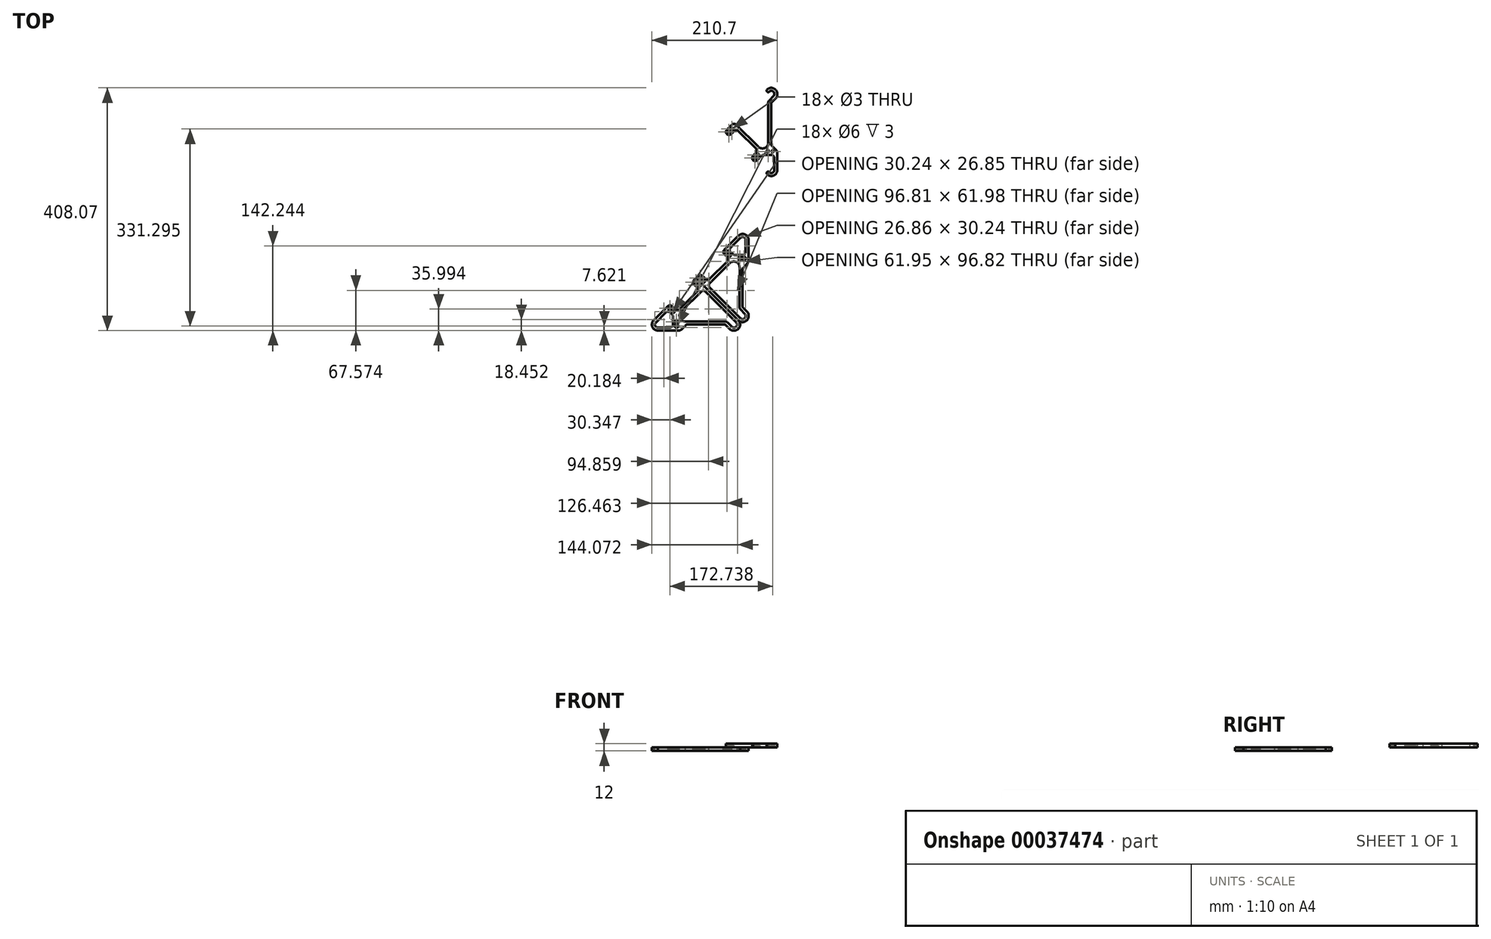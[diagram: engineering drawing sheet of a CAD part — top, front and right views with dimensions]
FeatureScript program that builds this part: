
annotation { "Feature Type Name" : "Feature", "Feature Type Description" : "" }
export const myFeature = defineFeature(function(context is Context, id is Id, definition is map)
    precondition{}
    {
        {
            var Q0;
            Q0=qCreatedBy(makeId("Top.planeOp"),FACE);
            var sketch = newSketch(context, id + "F0", { "sketchPlane" : qUnion([Q0])});
            skLineSegment(sketch, "E0", {"start": v(-29.78, -43.68) * mm, "end": v(-29.78, -43.68) * mm, "construction": true});
            skLineSegment(sketch, "E1", {"start": v(-29.78, -50.68) * mm, "end": v(-29.78, -50.68) * mm, "construction": true});
            skCircle(sketch, "E2", {"center": v(-40.77, -19.32) * mm, "radius": 1.5 * mm, "construction": true});
            skCircle(sketch, "E3", {"center": v(-35.83, -24.28) * mm, "radius": 1.5 * mm, "construction": true});
            skCircle(sketch, "E4", {"center": v(-29.78, -49.09) * mm, "radius": 1.5 * mm});
            skCircle(sketch, "E5", {"center": v(8.01, 19.57) * mm, "radius": 1.5 * mm});
            skCircle(sketch, "E6", {"center": v(3.07, 24.51) * mm, "radius": 1.5 * mm});
            skPoint(sketch, "E7.visualSharp", {"position": v(-33.33, -49.63) * mm});
            skCircle(sketch, "E8", {"center": v(-40.77, -19.32) * mm, "radius": 3 * mm});
            skCircle(sketch, "E9", {"center": v(-35.83, -24.28) * mm, "radius": 3 * mm});
            skCircle(sketch, "E10", {"center": v(-29.78, -49.09) * mm, "radius": 3 * mm});
            skCircle(sketch, "E11", {"center": v(3.07, 24.51) * mm, "radius": 3 * mm});
            skCircle(sketch, "E12", {"center": v(8.01, 19.57) * mm, "radius": 3 * mm});
            skCircle(sketch, "E13", {"center": v(-29.78, -42.09) * mm, "radius": 3 * mm});
            skArc(sketch, "E14", {"start": v(-67.9, -39.36) * mm, "mid": v(-70.46, -50.28) * mm, "end": v(-61.27, -56.7) * mm});
            skLineSegment(sketch, "E15", {"start": v(-67.9, -39.36) * mm, "end": v(-44.25, -15.73) * mm});
            skLineSegment(sketch, "E16", {"start": v(-32.29, -20.75) * mm, "end": v(-37.03, -16) * mm});
            skLineSegment(sketch, "E17", {"start": v(-25.1, -20.87) * mm, "end": v(4.62, 8.82) * mm});
            skLineSegment(sketch, "E18", {"start": v(-32.29, -20.75) * mm, "end": v(-32.16, -20.87) * mm});
            skLineSegment(sketch, "E19", {"start": v(4.47, 16.03) * mm, "end": v(4.62, 15.89) * mm});
            skLineSegment(sketch, "E20", {"start": v(4.47, 16.03) * mm, "end": v(-0.47, 20.98) * mm});
            skLineSegment(sketch, "E21", {"start": v(6.6, 28.05) * mm, "end": v(74.24, -39.64) * mm});
            skArc(sketch, "E22.filletArc", {"start": v(-32.16, -20.87) * mm, "mid": v(-28.63, -22.34) * mm, "end": v(-25.1, -20.87) * mm});
            skArc(sketch, "E23.filletArc", {"start": v(4.62, 8.82) * mm, "mid": v(6.08, 12.35) * mm, "end": v(4.62, 15.89) * mm});
            skLineSegment(sketch, "E24", {"start": v(64.59, -56.7) * mm, "end": v(67.17, -56.7) * mm});
            skPoint(sketch, "E25.visualSharp", {"position": v(91.3, -56.7) * mm});
            skArc(sketch, "E25.filletArc", {"start": v(67.17, -56.7) * mm, "mid": v(76.4, -50.54) * mm, "end": v(74.24, -39.64) * mm});
            skPoint(sketch, "E26.newPointA", {"position": v(59.7, -46.7) * mm});
            skPoint(sketch, "E27.newPointA", {"position": v(-24.2, -46.7) * mm});
            skLineSegment(sketch, "E28", {"start": v(-73.24, -63.03) * mm, "end": v(81.04, -63.03) * mm});
            skLineSegment(sketch, "E29.0", {"start": v(-64.61, -43.15) * mm, "end": v(-47.87, -26.41) * mm});
            skLineSegment(sketch, "E30", {"start": v(61.05, -55.24) * mm, "end": v(53.99, -48.17) * mm});
            skLineSegment(sketch, "E31", {"start": v(-15.01, -48.17) * mm, "end": v(-22.1, -55.24) * mm});
            skPoint(sketch, "E32.visualSharp", {"position": v(52.52, -46.7) * mm});
            skArc(sketch, "E32.filletArc", {"start": v(53.99, -48.17) * mm, "mid": v(52.36, -47.09) * mm, "end": v(50.45, -46.7) * mm});
            skPoint(sketch, "E33.newPointB", {"position": v(-61.27, -56.7) * mm});
            skArc(sketch, "E33.filletArc", {"start": v(61.05, -55.24) * mm, "mid": v(62.67, -56.33) * mm, "end": v(64.59, -56.7) * mm});
            skLineSegment(sketch, "E34", {"start": v(-25.63, -56.7) * mm, "end": v(-61.27, -56.7) * mm});
            skPoint(sketch, "E35.visualSharp", {"position": v(-23.56, -56.7) * mm});
            skArc(sketch, "E35.filletArc", {"start": v(-25.63, -56.7) * mm, "mid": v(-23.71, -56.33) * mm, "end": v(-22.1, -55.24) * mm});
            skArc(sketch, "E36", {"start": v(-44.25, -15.73) * mm, "mid": v(-40.58, -14.3) * mm, "end": v(-37.03, -16) * mm});
            skCircle(sketch, "E37", {"center": v(-35.83, -24.28) * mm, "radius": 1.5 * mm});
            skCircle(sketch, "E38", {"center": v(-40.77, -19.32) * mm, "radius": 1.5 * mm});
            skCircle(sketch, "E39", {"center": v(-29.78, -42.09) * mm, "radius": 1.5 * mm});
            skArc(sketch, "E40", {"start": v(-0.47, 20.98) * mm, "mid": v(-0.47, 28.05) * mm, "end": v(6.6, 28.05) * mm});
            skLineSegment(sketch, "E41", {"start": v(63.42, -50.52) * mm, "end": v(56.08, -43.17) * mm});
            skPoint(sketch, "E42.visualSharp", {"position": v(54.61, -41.7) * mm});
            skArc(sketch, "E42.filletArc", {"start": v(56.08, -43.17) * mm, "mid": v(54.45, -42.08) * mm, "end": v(52.54, -41.7) * mm});
            skArc(sketch, "E43.0", {"start": v(67.17, -51.7) * mm, "mid": v(71.79, -48.62) * mm, "end": v(70.7, -43.17) * mm});
            skLineSegment(sketch, "E44", {"start": v(70.7, -43.17) * mm, "end": v(70.7, -43.17) * mm});
            skLineSegment(sketch, "E45", {"start": v(66.35, -51.7) * mm, "end": v(67.17, -51.7) * mm});
            skArc(sketch, "E46", {"start": v(66.35, -51.7) * mm, "mid": v(64.77, -51.4) * mm, "end": v(63.42, -50.52) * mm});
            skArc(sketch, "E47.filletArc", {"start": v(18.76, 8.81) * mm, "mid": v(15.22, 10.28) * mm, "end": v(11.69, 8.81) * mm});
            skArc(sketch, "E48.filletArc", {"start": v(-64.61, -43.15) * mm, "mid": v(-65.7, -48.6) * mm, "end": v(-61.08, -51.68) * mm});
            skLineSegment(sketch, "E49", {"start": v(18.76, 8.81) * mm, "end": v(70.7, -43.17) * mm});
            skLineSegment(sketch, "E50", {"start": v(-11.48, -46.7) * mm, "end": v(50.45, -46.7) * mm});
            skLineSegment(sketch, "E51", {"start": v(-21.78, -24.63) * mm, "end": v(11.69, 8.81) * mm});
            skLineSegment(sketch, "E52", {"start": v(-47.87, -26.41) * mm, "end": v(-47.75, -26.3) * mm});
            skLineSegment(sketch, "E53", {"start": v(-40.68, -26.3) * mm, "end": v(-37.28, -29.7) * mm});
            skLineSegment(sketch, "E54", {"start": v(-35.82, -33.23) * mm, "end": v(-35.82, -46.68) * mm});
            skPoint(sketch, "E55.visualSharp", {"position": v(-44.21, -22.76) * mm});
            skArc(sketch, "E55.filletArc", {"start": v(-40.68, -26.3) * mm, "mid": v(-44.21, -24.83) * mm, "end": v(-47.75, -26.3) * mm});
            skPoint(sketch, "E56.visualSharp", {"position": v(-35.82, -31.16) * mm});
            skArc(sketch, "E56.filletArc", {"start": v(-35.82, -33.23) * mm, "mid": v(-36.2, -31.32) * mm, "end": v(-37.28, -29.7) * mm});
            skLineSegment(sketch, "E57", {"start": v(-61.08, -51.68) * mm, "end": v(-40.82, -51.68) * mm});
            skPoint(sketch, "E58.visualSharp", {"position": v(-35.82, -51.68) * mm});
            skArc(sketch, "E58.filletArc", {"start": v(-40.82, -51.68) * mm, "mid": v(-37.28, -50.22) * mm, "end": v(-35.82, -46.68) * mm});
            skPoint(sketch, "E59.visualSharp", {"position": v(-13.55, -46.7) * mm});
            skArc(sketch, "E59.filletArc", {"start": v(-11.48, -46.7) * mm, "mid": v(-13.4, -47.09) * mm, "end": v(-15.01, -48.17) * mm});
            skArc(sketch, "E60", {"start": v(-21.78, -24.63) * mm, "mid": v(-23.98, -35.45) * mm, "end": v(-14.88, -41.7) * mm});
            skLineSegment(sketch, "E61", {"start": v(-14.88, -41.7) * mm, "end": v(52.54, -41.7) * mm});
            skSolve(sketch);
        }
        {
            var Q0;
            Q0=makeQuery(id+"F0.imprint","IMPRINT",FACE,{"disambiguationData":[TD([[makeQuery(id+"F0.imprint","IMPRINT",EDGE,{"derivedFrom":sQuery(id+"F0.wireOp",EDGE,"ZM41ytca-vthh-FzDY-ZHJl-nfqRgOJDo8si")}),1.0]])]});
            var Q1;
            {var subQ2=sQuery(id+"F0.wireOp",EDGE,"462530cd-ab40-49ed-864a-d079afbf469e");var subQ6=sQuery(id+"F0.wireOp",EDGE,"E8");var subQ8=makeQuery(id+"F0.imprint","INTERSECT",VERTEX,{"disambiguationData":[OD(0.0)],"derivedFrom":[subQ6,subQ2]});Q1=makeQuery(id+"F0.imprint","IMPRINT",FACE,{"disambiguationData":[TD([[makeQuery(id+"F0.imprint","IMPRINT",EDGE,{"disambiguationData":[TD([[subQ8,-1.0]])],"derivedFrom":subQ6}),-1.0]])]});}
            var Q2;
            {var subQ0=sQuery(id+"F0.wireOp",EDGE,"462530cd-ab40-49ed-864a-d079afbf469e");var subQ1=sQuery(id+"F0.wireOp",EDGE,"E8");var subQ2=makeQuery(id+"F0.imprint","INTERSECT",VERTEX,{"disambiguationData":[OD(0.0)],"derivedFrom":[subQ1,subQ0]});Q2=makeQuery(id+"F0.imprint","IMPRINT",FACE,{"disambiguationData":[TD([[makeQuery(id+"F0.imprint","IMPRINT",EDGE,{"disambiguationData":[TD([[subQ2,-1.0]])],"derivedFrom":subQ1}),1.0]])]});}
            var Q3;
            {var subQ2=sQuery(id+"F0.wireOp",EDGE,"c8d69f50-1bdd-4b81-bc52-8b5ed8a16678");var subQ4=sQuery(id+"F0.wireOp",EDGE,"E9");var subQ6=makeQuery(id+"F0.imprint","INTERSECT",VERTEX,{"disambiguationData":[OD(0.0)],"derivedFrom":[subQ4,subQ2]});Q3=makeQuery(id+"F0.imprint","IMPRINT",FACE,{"disambiguationData":[TD([[makeQuery(id+"F0.imprint","IMPRINT",EDGE,{"disambiguationData":[TD([[subQ6,-1.0]])],"derivedFrom":subQ4}),-1.0]])]});}
            var Q4;
            {var subQ0=sQuery(id+"F0.wireOp",EDGE,"c8d69f50-1bdd-4b81-bc52-8b5ed8a16678");var subQ1=sQuery(id+"F0.wireOp",EDGE,"E9");var subQ2=makeQuery(id+"F0.imprint","INTERSECT",VERTEX,{"disambiguationData":[OD(0.0)],"derivedFrom":[subQ1,subQ0]});Q4=makeQuery(id+"F0.imprint","IMPRINT",FACE,{"disambiguationData":[TD([[makeQuery(id+"F0.imprint","IMPRINT",EDGE,{"disambiguationData":[TD([[subQ2,-1.0]])],"derivedFrom":subQ1}),1.0]])]});}
            var Q5;
            {var subQ3=sQuery(id+"F0.wireOp",EDGE,"462530cd-ab40-49ed-864a-d079afbf469e");var subQ5=sQuery(id+"F0.wireOp",EDGE,"E8");var subQ6=makeQuery(id+"F0.imprint","INTERSECT",VERTEX,{"disambiguationData":[OD(0.0)],"derivedFrom":[subQ5,subQ3]});Q5=makeQuery(id+"F0.imprint","IMPRINT",FACE,{"disambiguationData":[TD([[makeQuery(id+"F0.imprint","IMPRINT",EDGE,{"disambiguationData":[TD([[subQ6,1.0]])],"derivedFrom":subQ5}),-1.0]])]});}
            var Q6;
            {var subQ0=sQuery(id+"F0.wireOp",EDGE,"E16");Q6=makeQuery(id+"F0.imprint","IMPRINT",FACE,{"disambiguationData":[TD([[makeQuery(id+"F0.imprint","IMPRINT",EDGE,{"derivedFrom":subQ0}),1.0]])]});}
            var Q7;
            {var subQ0=sQuery(id+"F0.wireOp",EDGE,"462530cd-ab40-49ed-864a-d079afbf469e");var subQ1=sQuery(id+"F0.wireOp",EDGE,"E8");var subQ2=makeQuery(id+"F0.imprint","INTERSECT",VERTEX,{"disambiguationData":[OD(0.0)],"derivedFrom":[subQ1,subQ0]});Q7=makeQuery(id+"F0.imprint","IMPRINT",FACE,{"disambiguationData":[TD([[makeQuery(id+"F0.imprint","IMPRINT",EDGE,{"disambiguationData":[TD([[subQ2,1.0]])],"derivedFrom":subQ1}),1.0]])]});}
            var Q8;
            {var subQ0=sQuery(id+"F0.wireOp",EDGE,"c8d69f50-1bdd-4b81-bc52-8b5ed8a16678");var subQ1=sQuery(id+"F0.wireOp",EDGE,"E9");var subQ2=makeQuery(id+"F0.imprint","INTERSECT",VERTEX,{"disambiguationData":[OD(0.0)],"derivedFrom":[subQ1,subQ0]});Q8=makeQuery(id+"F0.imprint","IMPRINT",FACE,{"disambiguationData":[TD([[makeQuery(id+"F0.imprint","IMPRINT",EDGE,{"disambiguationData":[TD([[subQ2,1.0]])],"derivedFrom":subQ1}),1.0]])]});}
            var Q9;
            {var subQ0=sQuery(id+"F0.wireOp",EDGE,"e0227538-d441-4e94-826a-84f47eb18c94");var subQ1=makeQuery(id+"F0.imprint","INTERSECT",VERTEX,{"derivedFrom":[sQuery(id+"F0.wireOp",EDGE,"E10"),subQ0]});Q9=makeQuery(id+"F0.imprint","IMPRINT",FACE,{"disambiguationData":[TD([[makeQuery(id+"F0.imprint","IMPRINT",EDGE,{"disambiguationData":[TD([[subQ1,1.0]])],"derivedFrom":subQ0}),1.0]])]});}
            var Q10;
            Q10=makeQuery(id+"F0.imprint","IMPRINT",FACE,{"disambiguationData":[TD([[makeQuery(id+"F0.imprint","IMPRINT",EDGE,{"derivedFrom":sQuery(id+"F0.wireOp",EDGE,"E13")}),1.0]])]});
            var Q11;
            {var subQ0=sQuery(id+"F0.wireOp",EDGE,"E20");Q11=makeQuery(id+"F0.imprint","IMPRINT",FACE,{"disambiguationData":[TD([[makeQuery(id+"F0.imprint","IMPRINT",EDGE,{"derivedFrom":subQ0}),-1.0]])]});}
            var Q12;
            {var subQ2=sQuery(id+"F0.wireOp",EDGE,"98726ccb-f84b-485e-b86c-f66cbd653361");var subQ4=sQuery(id+"F0.wireOp",EDGE,"E12");var subQ6=makeQuery(id+"F0.imprint","INTERSECT",VERTEX,{"disambiguationData":[OD(0.0)],"derivedFrom":[subQ4,subQ2]});Q12=makeQuery(id+"F0.imprint","IMPRINT",FACE,{"disambiguationData":[TD([[makeQuery(id+"F0.imprint","IMPRINT",EDGE,{"disambiguationData":[TD([[subQ6,-1.0]])],"derivedFrom":subQ4}),-1.0]])]});}
            var Q13;
            {var subQ3=sQuery(id+"F0.wireOp",EDGE,"c5cb0bc4-31c7-4bfb-88ff-cc8c739e518f");var subQ7=sQuery(id+"F0.wireOp",EDGE,"E11");var subQ8=makeQuery(id+"F0.imprint","INTERSECT",VERTEX,{"disambiguationData":[OD(0.0)],"derivedFrom":[subQ7,subQ3]});Q13=makeQuery(id+"F0.imprint","IMPRINT",FACE,{"disambiguationData":[TD([[makeQuery(id+"F0.imprint","IMPRINT",EDGE,{"disambiguationData":[TD([[subQ8,1.0]])],"derivedFrom":subQ7}),-1.0]])]});}
            var Q14;
            {var subQ2=sQuery(id+"F0.wireOp",EDGE,"c5cb0bc4-31c7-4bfb-88ff-cc8c739e518f");var subQ6=sQuery(id+"F0.wireOp",EDGE,"E11");var subQ7=makeQuery(id+"F0.imprint","INTERSECT",VERTEX,{"disambiguationData":[OD(0.0)],"derivedFrom":[subQ6,subQ2]});Q14=makeQuery(id+"F0.imprint","IMPRINT",FACE,{"disambiguationData":[TD([[makeQuery(id+"F0.imprint","IMPRINT",EDGE,{"disambiguationData":[TD([[subQ7,-1.0]])],"derivedFrom":subQ6}),-1.0]])]});}
            var Q15;
            {var subQ0=sQuery(id+"F0.wireOp",EDGE,"E21");var subQ1=sQuery(id+"F0.wireOp",EDGE,"98726ccb-f84b-485e-b86c-f66cbd653361");var subQ2=makeQuery(id+"F0.imprint","INTERSECT",VERTEX,{"derivedFrom":[subQ1,subQ0]});Q15=makeQuery(id+"F0.imprint","IMPRINT",FACE,{"disambiguationData":[TD([[makeQuery(id+"F0.imprint","IMPRINT",EDGE,{"disambiguationData":[TD([[subQ2,1.0]])],"derivedFrom":subQ1}),-1.0]])]});}
            var Q16;
            {var subQ0=sQuery(id+"F0.wireOp",EDGE,"98726ccb-f84b-485e-b86c-f66cbd653361");var subQ1=sQuery(id+"F0.wireOp",EDGE,"E12");var subQ2=makeQuery(id+"F0.imprint","INTERSECT",VERTEX,{"disambiguationData":[OD(0.0)],"derivedFrom":[subQ1,subQ0]});Q16=makeQuery(id+"F0.imprint","IMPRINT",FACE,{"disambiguationData":[TD([[makeQuery(id+"F0.imprint","IMPRINT",EDGE,{"disambiguationData":[TD([[subQ2,1.0]])],"derivedFrom":subQ1}),1.0]])]});}
            var Q17;
            {var subQ0=sQuery(id+"F0.wireOp",EDGE,"c5cb0bc4-31c7-4bfb-88ff-cc8c739e518f");var subQ1=sQuery(id+"F0.wireOp",EDGE,"E11");var subQ2=makeQuery(id+"F0.imprint","INTERSECT",VERTEX,{"disambiguationData":[OD(0.0)],"derivedFrom":[subQ1,subQ0]});Q17=makeQuery(id+"F0.imprint","IMPRINT",FACE,{"disambiguationData":[TD([[makeQuery(id+"F0.imprint","IMPRINT",EDGE,{"disambiguationData":[TD([[subQ2,1.0]])],"derivedFrom":subQ1}),1.0]])]});}
            var Q18;
            Q18=makeQuery(id+"F0.imprint","IMPRINT",FACE,{"disambiguationData":[TD([[makeQuery(id+"F0.imprint","IMPRINT",EDGE,{"derivedFrom":sQuery(id+"F0.wireOp",EDGE,"E9")}),1.0]])]});
            var Q19;
            Q19=makeQuery(id+"F0.imprint","IMPRINT",FACE,{"disambiguationData":[TD([[makeQuery(id+"F0.imprint","IMPRINT",EDGE,{"derivedFrom":sQuery(id+"F0.wireOp",EDGE,"E4")}),-1.0]])]});
            var Q20;
            Q20=makeQuery(id+"F0.imprint","IMPRINT",FACE,{"disambiguationData":[TD([[makeQuery(id+"F0.imprint","IMPRINT",EDGE,{"derivedFrom":sQuery(id+"F0.wireOp",EDGE,"E8")}),1.0]])]});
            var Q21;
            {var subQ0=sQuery(id+"F0.wireOp",EDGE,"c5cb0bc4-31c7-4bfb-88ff-cc8c739e518f");var subQ1=sQuery(id+"F0.wireOp",EDGE,"E11");var subQ2=makeQuery(id+"F0.imprint","INTERSECT",VERTEX,{"disambiguationData":[OD(0.0)],"derivedFrom":[subQ1,subQ0]});Q21=makeQuery(id+"F0.imprint","IMPRINT",FACE,{"disambiguationData":[TD([[makeQuery(id+"F0.imprint","IMPRINT",EDGE,{"disambiguationData":[TD([[subQ2,-1.0]])],"derivedFrom":subQ1}),1.0]])]});}
            var Q22;
            Q22=makeQuery(id+"F0.imprint","IMPRINT",FACE,{"disambiguationData":[TD([[makeQuery(id+"F0.imprint","IMPRINT",EDGE,{"derivedFrom":sQuery(id+"F0.wireOp",EDGE,"E6")}),-1.0]])]});
            var Q23;
            Q23=makeQuery(id+"F0.imprint","IMPRINT",FACE,{"disambiguationData":[TD([[makeQuery(id+"F0.imprint","IMPRINT",EDGE,{"derivedFrom":sQuery(id+"F0.wireOp",EDGE,"E5")}),-1.0]])]});
            extrude(context, id + "F1", {"entities" : qUnion([Q0, Q1, Q2, Q3, Q4, Q5, Q6, Q7, Q8, Q9, Q10, Q11, Q12, Q13, Q14, Q15, Q16, Q17, Q18, Q19, Q20, Q21, Q22, Q23]), "depth" : 6 * mm});
        }
        {
            var Q0;
            Q0=makeQuery(id+"F0.imprint","IMPRINT",FACE,{"disambiguationData":[TD([[makeQuery(id+"F0.imprint","IMPRINT",EDGE,{"derivedFrom":sQuery(id+"F0.wireOp",EDGE,"E5")}),-1.0]])]});
            var Q1;
            Q1=makeQuery(id+"F0.imprint","IMPRINT",FACE,{"disambiguationData":[TD([[makeQuery(id+"F0.imprint","IMPRINT",EDGE,{"derivedFrom":sQuery(id+"F0.wireOp",EDGE,"E6")}),-1.0]])]});
            var Q2;
            Q2=makeQuery(id+"F0.imprint","IMPRINT",FACE,{"disambiguationData":[TD([[makeQuery(id+"F0.imprint","IMPRINT",EDGE,{"derivedFrom":sQuery(id+"F0.wireOp",EDGE,"E9")}),1.0]])]});
            var Q3;
            Q3=makeQuery(id+"F0.imprint","IMPRINT",FACE,{"disambiguationData":[TD([[makeQuery(id+"F0.imprint","IMPRINT",EDGE,{"derivedFrom":sQuery(id+"F0.wireOp",EDGE,"E8")}),1.0]])]});
            var Q4;
            Q4=makeQuery(id+"F0.imprint","IMPRINT",FACE,{"disambiguationData":[TD([[makeQuery(id+"F0.imprint","IMPRINT",EDGE,{"derivedFrom":sQuery(id+"F0.wireOp",EDGE,"E13")}),1.0]])]});
            var Q5;
            Q5=makeQuery(id+"F0.imprint","IMPRINT",FACE,{"disambiguationData":[TD([[makeQuery(id+"F0.imprint","IMPRINT",EDGE,{"derivedFrom":sQuery(id+"F0.wireOp",EDGE,"E4")}),-1.0]])]});
            extrude(context, id + "F2", {"entities" : qUnion([Q0, Q1, Q2, Q3, Q4, Q5]), "operationType" : NewBodyOperationType.REMOVE, "depth" : 3 * mm});
        }
        {
            var Q0;
            Q0=makeQuery(id+"F1.opExtrude","SWEPT_BODY",BODY,{"disambiguationData":[OSD([sQuery(id+"F0.wireOp",EDGE,"E4"),sQuery(id+"F0.wireOp",EDGE,"E5"),sQuery(id+"F0.wireOp",EDGE,"E6"),sQuery(id+"F0.wireOp",EDGE,"E14"),sQuery(id+"F0.wireOp",EDGE,"E15"),sQuery(id+"F0.wireOp",EDGE,"ZM41ytca-vthh-FzDY-ZHJl-nfqRgOJDo8si"),sQuery(id+"F0.wireOp",EDGE,"E16"),sQuery(id+"F0.wireOp",EDGE,"E17"),sQuery(id+"F0.wireOp",EDGE,"E18"),sQuery(id+"F0.wireOp",EDGE,"E19"),sQuery(id+"F0.wireOp",EDGE,"E20"),sQuery(id+"F0.wireOp",EDGE,"E21"),sQuery(id+"F0.wireOp",EDGE,"E22.filletArc"),sQuery(id+"F0.wireOp",EDGE,"E23.filletArc"),sQuery(id+"F0.wireOp",EDGE,"E24"),sQuery(id+"F0.wireOp",EDGE,"E25.filletArc"),sQuery(id+"F0.wireOp",EDGE,"E29.0"),sQuery(id+"F0.wireOp",EDGE,"Tq16YHEO-ABVa-SyG2-9Bo8-AwoXV9SY9UKx"),sQuery(id+"F0.wireOp",EDGE,"945284af-3b99-493e-8cb3-1405ac220aff.0"),sQuery(id+"F0.wireOp",EDGE,"oyrioEal-kBm6-h2JP-SiMW-HS9MCFllnOTl"),sQuery(id+"F0.wireOp",EDGE,"ebae724b-c969-4c6c-9507-989b8c4a6846.filletArc"),sQuery(id+"F0.wireOp",EDGE,"LpfddLv8-kVTz-Fq9e-9kgw-cFMKpV3D2Iyk"),sQuery(id+"F0.wireOp",EDGE,"93116c20-6c3f-4f09-9b0c-87327ea6eb7f.filletArc"),sQuery(id+"F0.wireOp",EDGE,"eb20cd87-545a-4932-9808-00091d9abf87.filletArc"),sQuery(id+"F0.wireOp",EDGE,"nxfSxcnj-Uu93-61Sm-abPP-Qb7fdRDBaPEy"),sQuery(id+"F0.wireOp",EDGE,"E30"),sQuery(id+"F0.wireOp",EDGE,"xg4YAkpb-tE1s-EWDx-Hdg8-UNIJCbS68nVv"),sQuery(id+"F0.wireOp",EDGE,"E31"),sQuery(id+"F0.wireOp",EDGE,"E32.filletArc"),sQuery(id+"F0.wireOp",EDGE,"E33.filletArc"),sQuery(id+"F0.wireOp",EDGE,"0bd198bb-c4ad-48d3-9048-f5a1ef5a0555.filletArc"),sQuery(id+"F0.wireOp",EDGE,"E34"),sQuery(id+"F0.wireOp",EDGE,"E35.filletArc"),sQuery(id+"F0.wireOp",EDGE,"E36"),sQuery(id+"F0.wireOp",EDGE,"E37"),sQuery(id+"F0.wireOp",EDGE,"E38"),sQuery(id+"F0.wireOp",EDGE,"E39"),sQuery(id+"F0.wireOp",EDGE,"E40"),sQuery(id+"F0.wireOp",EDGE,"E41"),sQuery(id+"F0.wireOp",EDGE,"E42.filletArc"),sQuery(id+"F0.wireOp",EDGE,"E43.0"),sQuery(id+"F0.wireOp",EDGE,"SPg3lbto-ea1S-YeVD-f8W7-4049b7SKFJDl"),sQuery(id+"F0.wireOp",EDGE,"E44"),sQuery(id+"F0.wireOp",EDGE,"E45"),sQuery(id+"F0.wireOp",EDGE,"E46"),sQuery(id+"F0.wireOp",EDGE,"E6A5n6ed-bLnf-SceK-tcdF-HIsw11yMVnoH"),sQuery(id+"F0.wireOp",EDGE,"e5Lx3FfZ-uw1w-XDj5-0S7D-BukahC8YTdbP"),sQuery(id+"F0.wireOp",EDGE,"E47.filletArc"),sQuery(id+"F0.wireOp",EDGE,"0ssyGrfO-lhhZ-gWxP-UVjv-oZQgXaOmNXYf"),sQuery(id+"F0.wireOp",EDGE,"KIXIkL1Q-xUR3-aLeU-v44d-RgIIkf4mlIdz"),sQuery(id+"F0.wireOp",EDGE,"2ec3d0ef-c9eb-4d0e-a1cf-228775a54ac2.filletArc"),sQuery(id+"F0.wireOp",EDGE,"E48.filletArc")])]});
            var Q1;
            Q1=qCreatedBy(makeId("Top.planeOp"),FACE);
            mirror(context, id + "F3", {"entities" : qUnion([Q0]), "mirrorPlane" : qUnion([Q1])});
        }
        {
            var Q0;
            Q0=makeQuery(id+"F1.opExtrude","SWEPT_BODY",BODY,{"disambiguationData":[OSD([sQuery(id+"F0.wireOp",EDGE,"E4"),sQuery(id+"F0.wireOp",EDGE,"E5"),sQuery(id+"F0.wireOp",EDGE,"E6"),sQuery(id+"F0.wireOp",EDGE,"E14"),sQuery(id+"F0.wireOp",EDGE,"E15"),sQuery(id+"F0.wireOp",EDGE,"ZM41ytca-vthh-FzDY-ZHJl-nfqRgOJDo8si"),sQuery(id+"F0.wireOp",EDGE,"E16"),sQuery(id+"F0.wireOp",EDGE,"E17"),sQuery(id+"F0.wireOp",EDGE,"E18"),sQuery(id+"F0.wireOp",EDGE,"E19"),sQuery(id+"F0.wireOp",EDGE,"E20"),sQuery(id+"F0.wireOp",EDGE,"E21"),sQuery(id+"F0.wireOp",EDGE,"E22.filletArc"),sQuery(id+"F0.wireOp",EDGE,"E23.filletArc"),sQuery(id+"F0.wireOp",EDGE,"E24"),sQuery(id+"F0.wireOp",EDGE,"E25.filletArc"),sQuery(id+"F0.wireOp",EDGE,"E29.0"),sQuery(id+"F0.wireOp",EDGE,"Tq16YHEO-ABVa-SyG2-9Bo8-AwoXV9SY9UKx"),sQuery(id+"F0.wireOp",EDGE,"945284af-3b99-493e-8cb3-1405ac220aff.0"),sQuery(id+"F0.wireOp",EDGE,"oyrioEal-kBm6-h2JP-SiMW-HS9MCFllnOTl"),sQuery(id+"F0.wireOp",EDGE,"ebae724b-c969-4c6c-9507-989b8c4a6846.filletArc"),sQuery(id+"F0.wireOp",EDGE,"LpfddLv8-kVTz-Fq9e-9kgw-cFMKpV3D2Iyk"),sQuery(id+"F0.wireOp",EDGE,"93116c20-6c3f-4f09-9b0c-87327ea6eb7f.filletArc"),sQuery(id+"F0.wireOp",EDGE,"eb20cd87-545a-4932-9808-00091d9abf87.filletArc"),sQuery(id+"F0.wireOp",EDGE,"nxfSxcnj-Uu93-61Sm-abPP-Qb7fdRDBaPEy"),sQuery(id+"F0.wireOp",EDGE,"E30"),sQuery(id+"F0.wireOp",EDGE,"xg4YAkpb-tE1s-EWDx-Hdg8-UNIJCbS68nVv"),sQuery(id+"F0.wireOp",EDGE,"E31"),sQuery(id+"F0.wireOp",EDGE,"E32.filletArc"),sQuery(id+"F0.wireOp",EDGE,"E33.filletArc"),sQuery(id+"F0.wireOp",EDGE,"0bd198bb-c4ad-48d3-9048-f5a1ef5a0555.filletArc"),sQuery(id+"F0.wireOp",EDGE,"E34"),sQuery(id+"F0.wireOp",EDGE,"E35.filletArc"),sQuery(id+"F0.wireOp",EDGE,"E36"),sQuery(id+"F0.wireOp",EDGE,"E37"),sQuery(id+"F0.wireOp",EDGE,"E38"),sQuery(id+"F0.wireOp",EDGE,"E39"),sQuery(id+"F0.wireOp",EDGE,"E40"),sQuery(id+"F0.wireOp",EDGE,"E41"),sQuery(id+"F0.wireOp",EDGE,"E42.filletArc"),sQuery(id+"F0.wireOp",EDGE,"E43.0"),sQuery(id+"F0.wireOp",EDGE,"SPg3lbto-ea1S-YeVD-f8W7-4049b7SKFJDl"),sQuery(id+"F0.wireOp",EDGE,"E44"),sQuery(id+"F0.wireOp",EDGE,"E45"),sQuery(id+"F0.wireOp",EDGE,"E46"),sQuery(id+"F0.wireOp",EDGE,"E6A5n6ed-bLnf-SceK-tcdF-HIsw11yMVnoH"),sQuery(id+"F0.wireOp",EDGE,"e5Lx3FfZ-uw1w-XDj5-0S7D-BukahC8YTdbP"),sQuery(id+"F0.wireOp",EDGE,"E47.filletArc"),sQuery(id+"F0.wireOp",EDGE,"0ssyGrfO-lhhZ-gWxP-UVjv-oZQgXaOmNXYf"),sQuery(id+"F0.wireOp",EDGE,"KIXIkL1Q-xUR3-aLeU-v44d-RgIIkf4mlIdz"),sQuery(id+"F0.wireOp",EDGE,"2ec3d0ef-c9eb-4d0e-a1cf-228775a54ac2.filletArc"),sQuery(id+"F0.wireOp",EDGE,"E48.filletArc")])]});
            var Q1;
            Q1=makeQuery(id+"F1.opExtrude","CAP_EDGE",EDGE,{"disambiguationData":[OSD([sQuery(id+"F0.wireOp",EDGE,"E21")])],"isStart":true});
            transform(context, id + "F4", {"entities" : qUnion([Q0]), "transformType" : TransformType.ROTATION, "transformAxis" : qUnion([Q1]), "angle" : 180 * degree, "makeCopy" : false});
        }
        {
            var Q0;
            Q0=qCreatedBy(makeId("Top.planeOp"),FACE);
            var sketch = newSketch(context, id + "F5", { "sketchPlane" : qUnion([Q0])});
            skLineSegment(sketch, "E62", {"start": v(126.55, 244.41) * mm, "end": v(126.55, 244.41) * mm, "construction": true});
            skLineSegment(sketch, "E63", {"start": v(133.55, 244.41) * mm, "end": v(133.55, 244.41) * mm, "construction": true});
            skCircle(sketch, "E64", {"center": v(102.2, 233.42) * mm, "radius": 1.5 * mm, "construction": true});
            skCircle(sketch, "E65", {"center": v(107.15, 238.37) * mm, "radius": 1.5 * mm, "construction": true});
            skCircle(sketch, "E66", {"center": v(131.96, 244.41) * mm, "radius": 1.5 * mm});
            skCircle(sketch, "E67", {"center": v(63.31, 282.2) * mm, "radius": 1.5 * mm});
            skCircle(sketch, "E68", {"center": v(58.36, 277.26) * mm, "radius": 1.5 * mm});
            skPoint(sketch, "E69.visualSharp", {"position": v(132.5, 240.86) * mm});
            skCircle(sketch, "E70", {"center": v(102.2, 233.42) * mm, "radius": 3 * mm});
            skCircle(sketch, "E71", {"center": v(107.15, 238.37) * mm, "radius": 3 * mm});
            skCircle(sketch, "E72", {"center": v(131.96, 244.41) * mm, "radius": 3 * mm});
            skCircle(sketch, "E73", {"center": v(58.36, 277.26) * mm, "radius": 3 * mm});
            skCircle(sketch, "E74", {"center": v(63.31, 282.2) * mm, "radius": 3 * mm});
            skCircle(sketch, "E75", {"center": v(123.96, 244.41) * mm, "radius": 3 * mm});
            skArc(sketch, "E76", {"start": v(122.24, 206.3) * mm, "mid": v(133.15, 203.74) * mm, "end": v(139.58, 212.93) * mm});
            skLineSegment(sketch, "E77", {"start": v(103.62, 241.9) * mm, "end": v(98.87, 237.16) * mm});
            skLineSegment(sketch, "E78", {"start": v(103.75, 249.1) * mm, "end": v(74.06, 278.81) * mm});
            skLineSegment(sketch, "E79", {"start": v(103.62, 241.9) * mm, "end": v(103.75, 242.03) * mm});
            skLineSegment(sketch, "E80", {"start": v(66.85, 278.67) * mm, "end": v(67, 278.81) * mm});
            skLineSegment(sketch, "E81", {"start": v(66.85, 278.67) * mm, "end": v(61.9, 273.72) * mm});
            skLineSegment(sketch, "E82", {"start": v(54.83, 280.8) * mm, "end": v(63.46, 289.42) * mm});
            skArc(sketch, "E83.filletArc", {"start": v(103.75, 242.03) * mm, "mid": v(105.21, 245.57) * mm, "end": v(103.75, 249.1) * mm});
            skArc(sketch, "E84.filletArc", {"start": v(74.06, 278.81) * mm, "mid": v(70.53, 280.28) * mm, "end": v(67, 278.81) * mm});
            skLineSegment(sketch, "E85", {"start": v(139.58, 338.78) * mm, "end": v(139.58, 341.36) * mm});
            skPoint(sketch, "E86.visualSharp", {"position": v(139.58, 365.5) * mm});
            skArc(sketch, "E86.filletArc", {"start": v(139.58, 341.36) * mm, "mid": v(133.41, 350.6) * mm, "end": v(122.52, 348.44) * mm});
            skPoint(sketch, "E87.newPointA", {"position": v(129.58, 333.89) * mm});
            skPoint(sketch, "E88.newPointA", {"position": v(129.58, 250) * mm});
            skLineSegment(sketch, "E89", {"start": v(145.9, 200.96) * mm, "end": v(145.9, 355.23) * mm});
            skLineSegment(sketch, "E90", {"start": v(138.12, 335.25) * mm, "end": v(131.05, 328.18) * mm});
            skLineSegment(sketch, "E91", {"start": v(131.05, 253.03) * mm, "end": v(138.12, 245.95) * mm});
            skPoint(sketch, "E92.visualSharp", {"position": v(129.58, 326.72) * mm});
            skArc(sketch, "E92.filletArc", {"start": v(131.05, 328.18) * mm, "mid": v(129.97, 326.56) * mm, "end": v(129.58, 324.65) * mm});
            skPoint(sketch, "E93.newPointB", {"position": v(139.58, 212.93) * mm});
            skArc(sketch, "E93.filletArc", {"start": v(138.12, 335.25) * mm, "mid": v(139.2, 336.87) * mm, "end": v(139.58, 338.78) * mm});
            skLineSegment(sketch, "E94", {"start": v(139.58, 242.42) * mm, "end": v(139.58, 212.93) * mm});
            skPoint(sketch, "E95.visualSharp", {"position": v(139.58, 244.49) * mm});
            skArc(sketch, "E95.filletArc", {"start": v(139.58, 242.42) * mm, "mid": v(139.2, 244.33) * mm, "end": v(138.12, 245.95) * mm});
            skCircle(sketch, "E96", {"center": v(107.15, 238.37) * mm, "radius": 1.5 * mm});
            skCircle(sketch, "E97", {"center": v(102.2, 233.42) * mm, "radius": 1.5 * mm});
            skCircle(sketch, "E98", {"center": v(123.96, 244.41) * mm, "radius": 1.5 * mm});
            skArc(sketch, "E99", {"start": v(61.9, 273.72) * mm, "mid": v(54.82, 273.73) * mm, "end": v(54.83, 280.8) * mm});
            skLineSegment(sketch, "E100", {"start": v(133.4, 337.62) * mm, "end": v(126.04, 330.27) * mm});
            skPoint(sketch, "E101.visualSharp", {"position": v(124.58, 328.8) * mm});
            skArc(sketch, "E101.filletArc", {"start": v(126.04, 330.27) * mm, "mid": v(124.96, 328.65) * mm, "end": v(124.58, 326.73) * mm});
            skArc(sketch, "E102.0", {"start": v(134.58, 341.36) * mm, "mid": v(131.5, 345.98) * mm, "end": v(126.05, 344.9) * mm});
            skLineSegment(sketch, "E103", {"start": v(126.05, 344.9) * mm, "end": v(126.05, 344.9) * mm});
            skLineSegment(sketch, "E104", {"start": v(134.58, 340.55) * mm, "end": v(134.58, 341.36) * mm});
            skArc(sketch, "E105", {"start": v(134.58, 340.55) * mm, "mid": v(134.28, 338.97) * mm, "end": v(133.4, 337.62) * mm});
            skArc(sketch, "E106.filletArc", {"start": v(126.02, 209.58) * mm, "mid": v(131.47, 208.5) * mm, "end": v(134.56, 213.12) * mm});
            skLineSegment(sketch, "E107", {"start": v(129.58, 256.56) * mm, "end": v(129.58, 324.65) * mm});
            skLineSegment(sketch, "E108", {"start": v(107.5, 252.42) * mm, "end": v(74.06, 285.88) * mm});
            skLineSegment(sketch, "E109", {"start": v(109.22, 233.47) * mm, "end": v(112.53, 236.86) * mm, "construction": true});
            skLineSegment(sketch, "E110", {"start": v(116.1, 238.38) * mm, "end": v(129.56, 238.38) * mm});
            skPoint(sketch, "E111.visualSharp", {"position": v(105.8, 229.94) * mm});
            skPoint(sketch, "E112.visualSharp", {"position": v(114, 238.38) * mm});
            skArc(sketch, "E112.filletArc", {"start": v(116.1, 238.38) * mm, "mid": v(114.16, 237.98) * mm, "end": v(112.53, 236.86) * mm});
            skLineSegment(sketch, "E113", {"start": v(134.56, 213.12) * mm, "end": v(134.56, 233.38) * mm});
            skPoint(sketch, "E114.visualSharp", {"position": v(134.56, 238.38) * mm});
            skArc(sketch, "E114.filletArc", {"start": v(134.56, 233.38) * mm, "mid": v(133.1, 236.91) * mm, "end": v(129.56, 238.38) * mm});
            skPoint(sketch, "E115.visualSharp", {"position": v(129.58, 254.5) * mm});
            skArc(sketch, "E115.filletArc", {"start": v(129.58, 256.56) * mm, "mid": v(129.96, 254.65) * mm, "end": v(131.05, 253.03) * mm});
            skArc(sketch, "E116", {"start": v(107.5, 252.42) * mm, "mid": v(118.33, 250.21) * mm, "end": v(124.58, 259.32) * mm});
            skLineSegment(sketch, "E117", {"start": v(124.58, 259.32) * mm, "end": v(124.58, 326.73) * mm});
            skLineSegment(sketch, "E118", {"start": v(74.06, 285.88) * mm, "end": v(70.53, 289.42) * mm});
            skPoint(sketch, "E119.visualSharp", {"position": v(67, 292.96) * mm});
            skArc(sketch, "E119.filletArc", {"start": v(70.53, 289.42) * mm, "mid": v(67, 290.89) * mm, "end": v(63.46, 289.42) * mm});
            skLineSegment(sketch, "E120", {"start": v(112.53, 236.86) * mm, "end": v(105.8, 229.94) * mm});
            skArc(sketch, "E121", {"start": v(98.6, 229.94) * mm, "mid": v(102.2, 228.42) * mm, "end": v(105.8, 229.94) * mm});
            skArc(sketch, "E122", {"start": v(98.87, 237.16) * mm, "mid": v(97.32, 233.6) * mm, "end": v(98.6, 229.94) * mm});
            skArc(sketch, "E123", {"start": v(122.52, 348.44) * mm, "mid": v(122.51, 344.9) * mm, "end": v(126.05, 344.9) * mm});
            skArc(sketch, "E124", {"start": v(126.02, 209.58) * mm, "mid": v(122.57, 209.74) * mm, "end": v(122.24, 206.3) * mm});
            skSolve(sketch);
        }
        {
            var Q0;
            Q0=makeQuery(id+"F5.imprint","IMPRINT",FACE,{"disambiguationData":[TD([[makeQuery(id+"F5.imprint","IMPRINT",EDGE,{"derivedFrom":sQuery(id+"F5.wireOp",EDGE,"E66")}),-1.0]])]});
            var Q1;
            Q1=makeQuery(id+"F5.imprint","IMPRINT",FACE,{"disambiguationData":[TD([[makeQuery(id+"F5.imprint","IMPRINT",EDGE,{"derivedFrom":sQuery(id+"F5.wireOp",EDGE,"E67")}),-1.0]])]});
            var Q2;
            Q2=makeQuery(id+"F5.imprint","IMPRINT",FACE,{"disambiguationData":[TD([[makeQuery(id+"F5.imprint","IMPRINT",EDGE,{"derivedFrom":sQuery(id+"F5.wireOp",EDGE,"E68")}),-1.0]])]});
            var Q3;
            Q3=makeQuery(id+"F5.imprint","IMPRINT",FACE,{"disambiguationData":[TD([[makeQuery(id+"F5.imprint","IMPRINT",EDGE,{"derivedFrom":sQuery(id+"F5.wireOp",EDGE,"E70")}),1.0]])]});
            var Q4;
            Q4=makeQuery(id+"F5.imprint","IMPRINT",FACE,{"disambiguationData":[TD([[makeQuery(id+"F5.imprint","IMPRINT",EDGE,{"derivedFrom":sQuery(id+"F5.wireOp",EDGE,"E71")}),1.0]])]});
            var Q5;
            Q5=makeQuery(id+"F5.imprint","IMPRINT",FACE,{"disambiguationData":[TD([[makeQuery(id+"F5.imprint","IMPRINT",EDGE,{"derivedFrom":sQuery(id+"F5.wireOp",EDGE,"E75")}),1.0]])]});
            var Q6;
            Q6=makeQuery(id+"F5.imprint","IMPRINT",FACE,{"disambiguationData":[TD([[makeQuery(id+"F5.imprint","IMPRINT",EDGE,{"derivedFrom":sQuery(id+"F5.wireOp",EDGE,"E70")}),-1.0]])]});
            extrude(context, id + "F6", {"entities" : qUnion([Q0, Q1, Q2, Q3, Q4, Q5, Q6]), "depth" : 6 * mm});
        }
        {
            var Q0;
            Q0=makeQuery(id+"F5.imprint","IMPRINT",FACE,{"disambiguationData":[TD([[makeQuery(id+"F5.imprint","IMPRINT",EDGE,{"derivedFrom":sQuery(id+"F5.wireOp",EDGE,"E68")}),-1.0]])]});
            var Q1;
            Q1=makeQuery(id+"F5.imprint","IMPRINT",FACE,{"disambiguationData":[TD([[makeQuery(id+"F5.imprint","IMPRINT",EDGE,{"derivedFrom":sQuery(id+"F5.wireOp",EDGE,"E67")}),-1.0]])]});
            var Q2;
            Q2=makeQuery(id+"F5.imprint","IMPRINT",FACE,{"disambiguationData":[TD([[makeQuery(id+"F5.imprint","IMPRINT",EDGE,{"derivedFrom":sQuery(id+"F5.wireOp",EDGE,"E71")}),1.0]])]});
            var Q3;
            Q3=makeQuery(id+"F5.imprint","IMPRINT",FACE,{"disambiguationData":[TD([[makeQuery(id+"F5.imprint","IMPRINT",EDGE,{"derivedFrom":sQuery(id+"F5.wireOp",EDGE,"E70")}),1.0]])]});
            var Q4;
            Q4=makeQuery(id+"F5.imprint","IMPRINT",FACE,{"disambiguationData":[TD([[makeQuery(id+"F5.imprint","IMPRINT",EDGE,{"derivedFrom":sQuery(id+"F5.wireOp",EDGE,"E75")}),1.0]])]});
            var Q5;
            Q5=makeQuery(id+"F5.imprint","IMPRINT",FACE,{"disambiguationData":[TD([[makeQuery(id+"F5.imprint","IMPRINT",EDGE,{"derivedFrom":sQuery(id+"F5.wireOp",EDGE,"E66")}),-1.0]])]});
            var Q6;
            Q6=sQuery(id+"F5.wireOp",EDGE,"E74");
            extrude(context, id + "F7", {"entities" : qUnion([Q0, Q1, Q2, Q3, Q4, Q5]), "operationType" : NewBodyOperationType.REMOVE, "surfaceEntities" : qUnion([Q6]), "depth" : 3 * mm});
        }
    });
